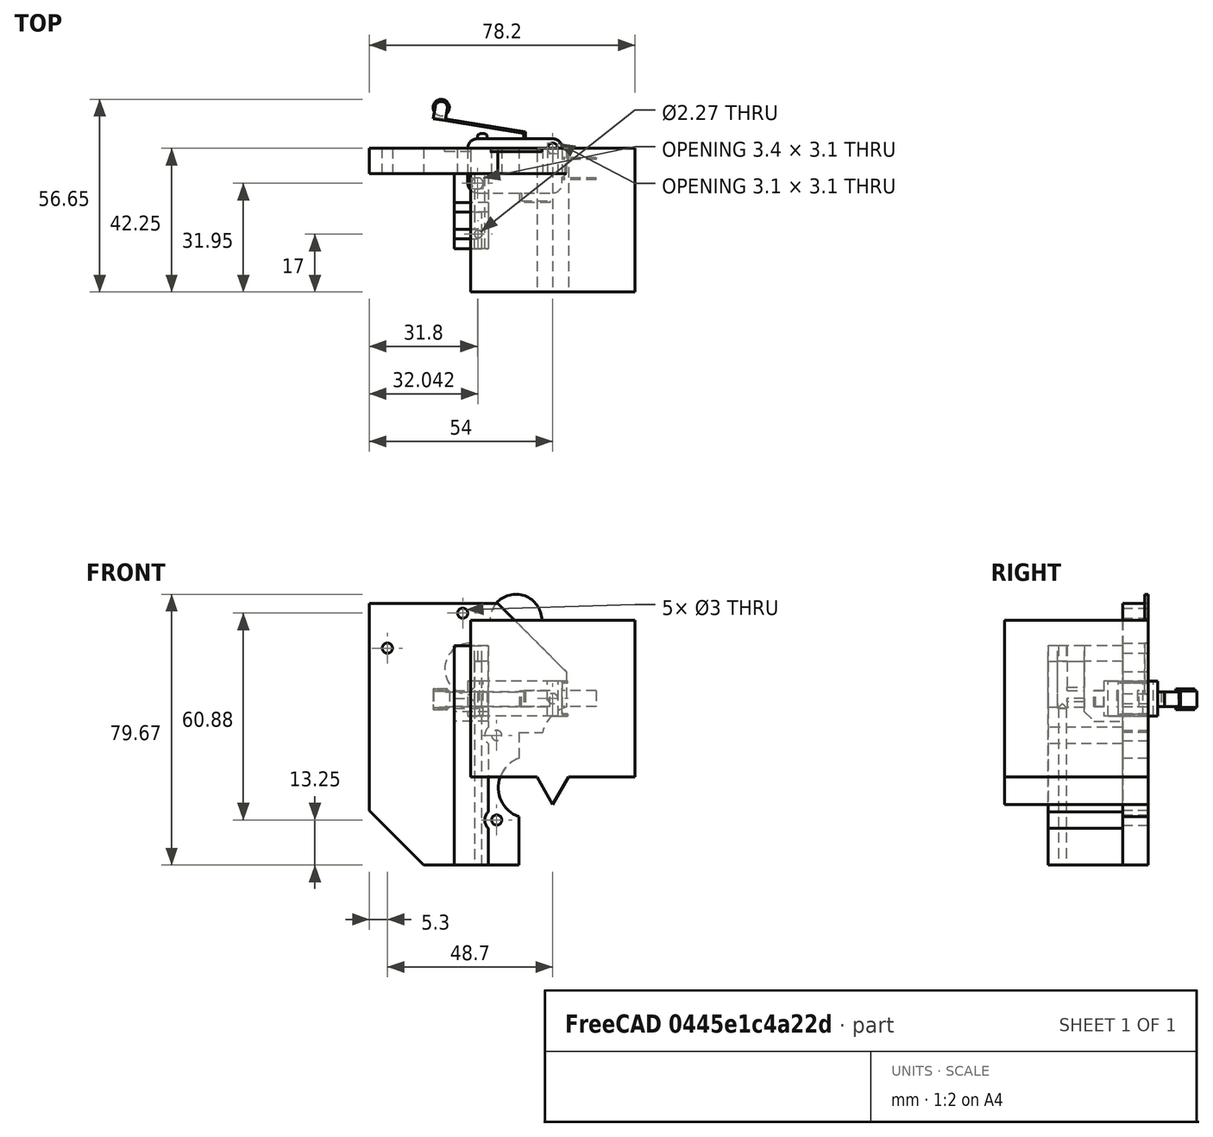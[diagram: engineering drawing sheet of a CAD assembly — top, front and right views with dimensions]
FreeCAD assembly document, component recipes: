
FREECAD ASSEMBLY — COMPONENT RECIPES ("no_touchy")

This assembly document has 5 components, labeled P0..P4 below (a component is one placed body or linked part). 2 of them carry a construction recipe — the FreeCAD feature program that regenerates the part from scratch, quoted from this document or its linked companion documents; the rest are supplied as boundary geometry only. No exploded tour is included for this assembly.
COMPONENT P0 — geometry summary ("allen"; no construction recipe available for this part):
  bounding box: 74.1 x 15.9 x 1.5 mm
  tessellated surface: 68 triangles
  volume: 478904856520590275852955231166615715246145621785509215956463249338484086506495282965888048924409776630849818438009607219283139737538738958728098922627072 mm^3 (27643994136273034751166802490876510581696525263799634684042413042340372770473193175274414860802890257049373180057316332820426398488878841318054540869632% of its bounding box)
  symmetry: mirror-symmetric across its z mid-plane
COMPONENT P1 — recipe-attached ("ender_3_fan_shroud", modeled in this document).
Construction recipe (the document's own serialized feature program — sketch geometry with constraints, then the solid features built on it; lengths are millimeters unless a unit is written):

FEATURE [Sketcher::SketchObject] Sketch004
  MapMode = 1
  Placement = pos=(0,0,0) rot=(1,0,0;1.5708rad)
  sketch-geometry (11):
    g0: LineSegment StartX=-24.2 StartY=23.075 StartZ=0 EndX=-18.45 EndY=23.075 EndZ=0
    g1: LineSegment StartX=24.2 StartY=23.075 StartZ=0 EndX=24.2 EndY=-23.075 EndZ=0
    g2: LineSegment StartX=24.2 StartY=-23.075 StartZ=0 EndX=4.67654 EndY=-23.075 EndZ=0
    g3: LineSegment StartX=-24.2 StartY=-23.075 StartZ=0 EndX=-24.2 EndY=1.125 EndZ=0
    g4: ArcOfCircle CenterX=-10.85 CenterY=23.075 CenterZ=0 NormalX=0 NormalY=0 NormalZ=1 AngleXU=0 Radius=7.6 StartAngle=0 EndAngle=3.14159
    g5: LineSegment StartX=-3.25 StartY=23.075 StartZ=0 EndX=24.2 EndY=23.075 EndZ=0
    g6: ArcOfCircle CenterX=-24.2 CenterY=8.725 CenterZ=0 NormalX=0 NormalY=0 NormalZ=1 AngleXU=0 Radius=7.6 StartAngle=1.5708 EndAngle=4.71239
    g7: LineSegment StartX=-24.2 StartY=16.325 StartZ=0 EndX=-24.2 EndY=23.075 EndZ=0
    g8: LineSegment StartX=-4.67654 StartY=-23.075 StartZ=0 EndX=5.338e-13 EndY=-31.175 EndZ=0
    g9: LineSegment StartX=4.67654 StartY=-23.075 StartZ=0 EndX=5.338e-13 EndY=-31.175 EndZ=0
    g10: LineSegment StartX=-4.67654 StartY=-23.075 StartZ=0 EndX=-24.2 EndY=-23.075 EndZ=0
  constraints (32):
    c: Coincident(g5,g1)
    c: Coincident(g1,g2)
    c: Coincident(g10,g3)
    c: Coincident(g7,g0)
    c: Horizontal(g0)
    c: Horizontal(g2)
    c: Vertical(g1)
    c: Vertical(g3)
    c: Tangent(g0,g5)
    c: Horizontal(g5,g4)
    c: Diameter(g4) = 15.2
    c: DistanceX(g0,g1) = 48.4
    c: Coincident(g4,g5)
    c: Coincident(g4,g0)
    c: PointOnObject(g6,g3)
    c: Coincident(g7,g6)
    c: Tangent(g3,g7)
    c: PointOnObject(g3,g6)
    c: Vertical(g6,g6)
    c: Diameter(g6) = 15.2
    c: DistanceY(g10,g0) = 46.15
    c: DistanceX(g0,g0) = 5.75
    c: DistanceY(g7,g7) = 6.75
    c: Coincident(g9,g8)
    c: Coincident(g2,g9)
    c: Coincident(g10,g8)
    c: Tangent(g2,g10)
    c: Angle(g9,g8) = 1.0472
    c: Equal(g9,g8)
    c: Distance(g8,g5) = 54.25
    c: Equal(g2,g10)
    c: Symmetric(g1,g3,g-1)
FEATURE [PartDesign::Pad] Pad001
  Length = 1
  Length2 = 100
  Placement = pos=(0,0,0) rot=(1,0,0;1.5708rad)
  Profile = -> Sketch004
  Type = 0
FEATURE [Sketcher::SketchObject] Sketch006
  ExternalGeometry = -> [Pad001]
  MapMode = 5
  Placement = pos=(0,-1,3e-16) rot=(1,0,0;1.5708rad)
  Support = -> [Pad001]
  sketch-geometry (7):
    g0: LineSegment StartX=-24.2 StartY=23.075 StartZ=0 EndX=24.2 EndY=23.075 EndZ=0
    g1: LineSegment StartX=24.2 StartY=23.075 StartZ=0 EndX=24.2 EndY=-23.075 EndZ=0
    g2: LineSegment StartX=-24.2 StartY=-23.075 StartZ=0 EndX=-24.2 EndY=23.075 EndZ=0
    g3: LineSegment StartX=-24.2 StartY=-23.075 StartZ=0 EndX=-4.67654 EndY=-23.075 EndZ=0
    g4: LineSegment StartX=-4.67654 StartY=-23.075 StartZ=0 EndX=5.338e-13 EndY=-31.175 EndZ=0
    g5: LineSegment StartX=5.338e-13 StartY=-31.175 StartZ=0 EndX=4.67654 EndY=-23.075 EndZ=0
    g6: LineSegment StartX=4.67654 StartY=-23.075 StartZ=0 EndX=24.2 EndY=-23.075 EndZ=0
  constraints (15):
    c: Coincident(g0,g1)
    c: Coincident(g2,g0)
    c: Horizontal(g0)
    c: Vertical(g1)
    c: Coincident(g2,g3)
    c: Coincident(g3,g4)
    c: Coincident(g4,g5)
    c: Coincident(g5,g6)
    c: Coincident(g6,g1)
    c: Coincident(g1,g-4)
    c: Coincident(g5,g-5)
    c: Coincident(g4,g-6)
    c: Coincident(g3,g-7)
    c: Coincident(g2,g-8)
    c: Coincident(g0,g-3)
FEATURE [PartDesign::Pad] Pad003
  BaseFeature = -> Pad001
  Length = 41.25
  Length2 = 100
  Placement = pos=(0,0,0) rot=(1,0,0;1.5708rad)
  Profile = -> Sketch006
  Type = 0
FEATURE [PartDesign::Body] Body001
  Group = -> [Pad001,Sketch004,Sketch006,Pad003]
  Origin = -> Origin009
  Tip = -> Pad003
COMPONENT P2 — geometry summary ("limit_switch"; no construction recipe available for this part):
  bounding box: 48.0 x 30.1 x 10.3 mm
  tessellated surface: 380 triangles
  volume: 10531229166886375367833218790467075027243968238796608645308768968464382942997063844467289304044690295309601693225177005043369266873093713751413007993119692917567389696 mm^3 (70759783561661155036835508914529565986221704150470811669326561292182287791302966392552419513098743421665918382326803244313745572390062196069500436793845928861630464% of its bounding box)
  symmetry: mirror-symmetric across its y mid-plane
COMPONENT P3 — geometry summary ("micro_swiss_direct_drive_backplate"; no construction recipe available for this part):
  bounding box: 90.8 x 60.0 x 3.2 mm
  tessellated surface: 128 triangles
  volume: 2873429139123541841188444806675058272103768550042216090270967831984327951100462688038986050576327031290007893351530426870904369629373984737226610461114368 mm^3 (16491213821775155754527166314603517383818518835042913780849936584284578971568722629976532881193366380947111070735649138382941081930098950302775747018752% of its bounding box)
  symmetry: mirror-symmetric across its y mid-plane
COMPONENT P4 — recipe-attached ("no_touchy", modeled in this document).
Construction recipe (the document's own serialized feature program — sketch geometry with constraints, then the solid features built on it; lengths are millimeters unless a unit is written):

FEATURE [Sketcher::SketchObject] Sketch005
  MapMode = 5
  Placement = pos=(0,0,0) rot=(1,0,0;1.5708rad)
  Support = -> [XZ_Plane008]
  expr: Constraints[40] = -1 * Spreadsheet.limit_switch_hole_offset_x
  expr: Constraints[41] = -1 * Spreadsheet.limit_switch_hole_offset_y - 3
  sketch-geometry (16):
    g0: LineSegment StartX=-10 StartY=-9.95247 StartZ=0 EndX=-10 EndY=-17.609 EndZ=0
    g1: LineSegment StartX=-10 StartY=-49 StartZ=0 EndX=-38 EndY=-49 EndZ=0
    g2: LineSegment StartX=-54 StartY=-33 StartZ=0 EndX=-54 EndY=28 EndZ=0
    g3: LineSegment StartX=-54 StartY=28 StartZ=0 EndX=-16.1525 EndY=28 EndZ=0
    g4: LineSegment StartX=-10 StartY=-34.7961 StartZ=0 EndX=-10 EndY=-49 EndZ=0
    g5: LineSegment StartX=-10 StartY=-9.95247 StartZ=0 EndX=-2.95564 EndY=-9.95247 EndZ=0
    g6: LineSegment StartX=4 StartY=7.84746 StartZ=0 EndX=4 EndY=-2.5 EndZ=0
    g7: Circle CenterX=0 CenterY=0 CenterZ=0 NormalX=0 NormalY=0 NormalZ=1 AngleXU=0 Radius=2.25
    g8: Circle CenterX=-16.5 CenterY=-10.87 CenterZ=0 NormalX=0 NormalY=0 NormalZ=1 AngleXU=0 Radius=2.25
    g9: Circle CenterX=-16.5 CenterY=-35.75 CenterZ=0 NormalX=0 NormalY=0 NormalZ=1 AngleXU=0 Radius=2.25
    g10: ArcOfCircle CenterX=6.97621 CenterY=-12.25 CenterZ=0 NormalX=0 NormalY=0 NormalZ=1 AngleXU=0 Radius=10.1941 StartAngle=1.86706 EndAngle=2.91426
    g11: ArcOfCircle CenterX=-6.87222 CenterY=-26.2026 CenterZ=0 NormalX=0 NormalY=0 NormalZ=1 AngleXU=0 Radius=9.14502 StartAngle=1.91986 EndAngle=4.36332
    g12: LineSegment StartX=-54 StartY=-33 StartZ=0 EndX=-38 EndY=-49 EndZ=0
    g13: LineSegment StartX=-16.1525 StartY=28 StartZ=0 EndX=4 EndY=7.84746 EndZ=0
    g14: Circle CenterX=-26.5 CenterY=25.13 CenterZ=0 NormalX=0 NormalY=0 NormalZ=1 AngleXU=0 Radius=2.25
    g15: Circle CenterX=-48.7 CenterY=14.83 CenterZ=0 NormalX=0 NormalY=0 NormalZ=1 AngleXU=0 Radius=2.25
  constraints (50):
    c: Coincident(g4,g1)
    c: Horizontal(g1)
    c: Vertical(g0)
    c: Vertical(g2)
    c: Horizontal(g3)
    c: Coincident(g3,g2)
    c: Coincident(g5,g0)
    c: Coincident(g10,g6)
    c: Coincident(g10,g5)
    c: Angle(g10) = 1.0472
    c: Vertical(g6)
    c: Horizontal(g5)
    c: DistanceX(g8) = -16.5
    c: DistanceY(g8) = -10.87
    c: Radius(g7) = 2.25
    c: Equal(g8,g7)
    c: DistanceX(g9) = -16.5
    c: DistanceY(g9) = -35.75
    c: Equal(g9,g7)
    c: Coincident(g11,g0)
    c: Angle(g11) = 2.44346
    c: Vertical(g4)
    c: Coincident(g4,g11)
    c: Vertical(g4,g0)
    c: DistanceX(g7) = 0
    c: DistanceY(g7) = 0
    c: DistanceX(g4) = -10
    c: DistanceY(g4) = -34.7961
    c: DistanceX(g11) = -6.87222
    c: DistanceX(g10) = 6.97621
    c: DistanceY(g10) = -12.25
    c: DistanceX(g6) = 4
    c: DistanceY(g6) = -2.5
    c: Coincident(g12,g2)
    c: Coincident(g12,g1)
    c: Angle(g1,g12) = 2.35619
    c: Coincident(g13,g3)
    c: Coincident(g13,g6)
    c: Angle(g3,g13) = 2.35619
    c: Equal(g14,g7)
    c: DistanceX(g14,g8) = 10
    c: DistanceY(g14,g8) = -36
    c: Equal(g15,g7)
    c: DistanceX(g15,g14) = 22.2
    c: DistanceY(g15,g14) = 10.3
    c: DistanceX(g2) = -54
    c: DistanceY(g2) = 28
    c: DistanceX(g1) = -38
    c: DistanceY(g1) = -49
    c: Distance(g13) = 28.5
FEATURE [PartDesign::Pad] Pad002
  Length = 7.5
  Length2 = 100
  Placement = pos=(0,0,0) rot=(1,0,0;1.5708rad)
  Profile = -> Sketch005
  Type = 0
  expr: Length = Spreadsheet.no_touchy_plate_mount_thickness
FEATURE [Sketcher::SketchObject] Sketch007
  ExternalGeometry = -> [Pad002]
  MapMode = 5
  Placement = pos=(0,-7.5,-1.7e-15) rot=(1,0,0;1.5708rad)
  Support = -> [Pad002]
  expr: Constraints[21] = Spreadsheet.no_touchy_allen_block_pad_width
  expr: Constraints[19] = Spreadsheet.no_touchy_allen_block_pad_length
  sketch-geometry (8):
    g0: LineSegment StartX=-29 StartY=15.5 StartZ=0 EndX=-19 EndY=15.5 EndZ=0
    g1: LineSegment StartX=-19 StartY=15.5 StartZ=0 EndX=-19 EndY=-8.42046 EndZ=0
    g2: LineSegment StartX=-19 StartY=-49 StartZ=0 EndX=-29 EndY=-49 EndZ=0
    g3: LineSegment StartX=-29 StartY=-49 StartZ=0 EndX=-29 EndY=15.5 EndZ=0
    g4: ArcOfCircle CenterX=-16.5 CenterY=-10.87 CenterZ=0 NormalX=0 NormalY=0 NormalZ=1 AngleXU=0 Radius=3.5 StartAngle=2.3664 EndAngle=3.91679
    g5: LineSegment StartX=-19 StartY=-13.3194 StartZ=0 EndX=-19 EndY=-33.3005 EndZ=0
    g6: ArcOfCircle CenterX=-16.5 CenterY=-35.75 CenterZ=0 NormalX=0 NormalY=0 NormalZ=1 AngleXU=0 Radius=3.5 StartAngle=2.3664 EndAngle=3.91679
    g7: LineSegment StartX=-19 StartY=-38.1995 StartZ=0 EndX=-19 EndY=-49 EndZ=0
  constraints (22):
    c: Coincident(g0,g1)
    c: Coincident(g7,g2)
    c: Coincident(g2,g3)
    c: Coincident(g3,g0)
    c: Horizontal(g0)
    c: Horizontal(g2)
    c: Vertical(g1)
    c: Vertical(g3)
    c: Horizontal(g2,g-3)
    c: Coincident(g4,g-5)
    c: Coincident(g1,g4)
    c: Coincident(g5,g4)
    c: Tangent(g1,g5)
    c: Coincident(g6,g-4)
    c: Coincident(g5,g6)
    c: Coincident(g7,g6)
    c: Tangent(g5,g7)
    c: Equal(g6,g4)
    c: Radius(g4) = 3.5
    c: DistanceY(g3,g3) = 64.5
    c: DistanceX(g0,g4) = 2.5
    c: DistanceX(g2,g2) = 10
FEATURE [PartDesign::Pad] Pad004
  BaseFeature = -> Pad002
  Length = 22
  Length2 = 100
  Placement = pos=(0,0,0) rot=(1,0,0;1.5708rad)
  Profile = -> Sketch007
  Type = 0
  expr: Length = Spreadsheet.no_touchy_allen_block_pad_height
FEATURE [Sketcher::SketchObject] Sketch008
  ExternalGeometry = -> [Pad004]
  MapMode = 5
  Placement = pos=(0,-1.09e-14,-49) rot=(1,0,0;3.14159rad)
  Support = -> [Pad004]
  expr: Constraints[0] = Spreadsheet.no_touchy_allen_hole_diameter
  sketch-geometry (1):
    g0: Circle CenterX=-21.958 CenterY=25.2495 CenterZ=0 NormalX=0 NormalY=0 NormalZ=1 AngleXU=0 Radius=1.135
  constraints (3):
    c: Diameter(g0) = 2.27
    c: DistanceX(g0,g-3) = 3.95804
    c: DistanceY(g0,g-3) = -25.2495
FEATURE [PartDesign::Pocket] Pocket001  label="Pocket_allen_hole"
  BaseFeature = -> Pad004
  Length = 1
  Length2 = 100
  Placement = pos=(0,0,0) rot=(1,0,0;1.5708rad)
  Profile = -> Sketch008
  Type = 1
FEATURE [Sketcher::SketchObject] Sketch009
  ExternalGeometry = -> [Pocket001]
  MapMode = 5
  Placement = pos=(0,-29.5,1e-16) rot=(1,0,0;1.5708rad)
  Support = -> [Pocket001]
  sketch-geometry (4):
    g0: LineSegment StartX=-20.823 StartY=11 StartZ=0 EndX=-23.093 EndY=11 EndZ=0
    g1: LineSegment StartX=-23.093 StartY=11 StartZ=0 EndX=-23.093 EndY=-1.5 EndZ=0
    g2: LineSegment StartX=-20.823 StartY=-1.5 StartZ=0 EndX=-20.823 EndY=11 EndZ=0
    g3: ArcOfCircle CenterX=-21.958 CenterY=-1.5 CenterZ=0 NormalX=0 NormalY=0 NormalZ=1 AngleXU=0 Radius=1.135 StartAngle=3.14159 EndAngle=6.28319
  constraints (13):
    c: Coincident(g0,g1)
    c: Coincident(g2,g0)
    c: Horizontal(g0)
    c: Vertical(g1)
    c: Vertical(g2)
    c: Vertical(g2,g-3)
    c: Vertical(g1,g-3)
    c: Coincident(g3,g2)
    c: Coincident(g3,g1)
    c: Horizontal(g2,g1)
    c: Horizontal(g1,g3)
    c: DistanceY(g-3,g1) = 47.5
    c: DistanceY(g-3,g0) = 60
FEATURE [PartDesign::Pocket] Pocket002  label="Pocket_allen_short_slot"
  BaseFeature = -> Pocket001
  Length = 22
  Length2 = 100
  Placement = pos=(0,0,0) rot=(1,0,0;1.5708rad)
  Profile = -> Sketch009
  Type = 0
  expr: Length = Spreadsheet.no_touchy_allen_block_pad_height
FEATURE [Sketcher::SketchObject] Sketch010
  ExternalGeometry = -> [Pocket002]
  MapMode = 5
  Placement = pos=(-19,0,0) rot=(0.707107,0,0.707107;3.14159rad)
  Support = -> [Pocket002]
  sketch-geometry (5):
    g0: LineSegment StartX=-3.85471 StartY=18.7661 StartZ=0 EndX=15.5 EndY=18.7661 EndZ=0
    g1: LineSegment StartX=15.5 StartY=18.7661 StartZ=0 EndX=15.5 EndY=7.5 EndZ=0
    g2: LineSegment StartX=15.5 StartY=7.5 StartZ=0 EndX=-6.68553 EndY=7.5 EndZ=0
    g3: LineSegment StartX=-6.68553 StartY=7.5 StartZ=0 EndX=-6.68553 EndY=15.9352 EndZ=0
    g4: LineSegment StartX=-6.68553 StartY=15.9352 StartZ=0 EndX=-3.85471 EndY=18.7661 EndZ=0
  constraints (12):
    c: Coincident(g1,g2)
    c: Horizontal(g0)
    c: Horizontal(g2)
    c: Vertical(g1)
    c: Vertical(g3)
    c: Coincident(g3,g2)
    c: Horizontal(g1,g-4)
    c: Coincident(g1,g0)
    c: Vertical(g1,g-4)
    c: Coincident(g3,g4)
    c: Coincident(g0,g4)
    c: Angle(g3,g4) = 2.35619
FEATURE [PartDesign::Pocket] Pocket003  label="Pocket_limit_switch_actuator"
  BaseFeature = -> Pocket002
  Length = 5
  Length2 = 100
  Placement = pos=(0,0,0) rot=(1,0,0;1.5708rad)
  Profile = -> Sketch010
  Type = 1
FEATURE [Sketcher::SketchObject] Sketch011
  ExternalGeometry = -> [Pocket003]
  MapMode = 5
  Placement = pos=(-29,0,0) rot=(0.707107,0,-0.707107;3.14159rad)
  Support = -> [Pocket003]
  sketch-geometry (4):
    g0: LineSegment StartX=-15.5 StartY=23.8145 StartZ=0 EndX=2.935 EndY=23.8145 EndZ=0
    g1: LineSegment StartX=2.935 StartY=23.8145 StartZ=0 EndX=2.935 EndY=26.6845 EndZ=0
    g2: LineSegment StartX=2.935 StartY=26.6845 StartZ=0 EndX=-15.5 EndY=26.6845 EndZ=0
    g3: LineSegment StartX=-15.5 StartY=26.6845 StartZ=0 EndX=-15.5 EndY=23.8145 EndZ=0
  constraints (7):
    c: Coincident(g0,g1)
    c: Coincident(g1,g2)
    c: Coincident(g2,g3)
    c: Coincident(g3,g0)
    c: Horizontal(g0)
    c: Vertical(g1)
    c: Vertical(g3)
FEATURE [PartDesign::Pocket] Pocket004  label="Pocket_allen_insert_1"
  BaseFeature = -> Pocket003
  Length = 7
  Length2 = 100
  Placement = pos=(0,0,0) rot=(1,0,0;1.5708rad)
  Profile = -> Sketch011
  Type = 0
FEATURE [Sketcher::SketchObject] Sketch012
  ExternalGeometry = -> [Pocket004]
  MapMode = 5
  Placement = pos=(-29,0,0) rot=(0.707107,0,-0.707107;3.14159rad)
  Support = -> [Pocket004]
  expr: Constraints[10] = Spreadsheet.no_touchy_allen_hole_diameter
  sketch-geometry (4):
    g0: LineSegment StartX=-2.335 StartY=18.7661 StartZ=0 EndX=-0.065 EndY=18.7661 EndZ=0
    g1: LineSegment StartX=-0.065 StartY=18.7661 StartZ=0 EndX=-0.065 EndY=23.8145 EndZ=0
    g2: LineSegment StartX=-0.065 StartY=23.8145 StartZ=0 EndX=-2.335 EndY=23.8145 EndZ=0
    g3: LineSegment StartX=-2.335 StartY=23.8145 StartZ=0 EndX=-2.335 EndY=18.7661 EndZ=0
  constraints (12):
    c: Coincident(g0,g1)
    c: Coincident(g1,g2)
    c: Coincident(g2,g3)
    c: Coincident(g3,g0)
    c: Horizontal(g0)
    c: Horizontal(g2)
    c: Vertical(g1)
    c: Vertical(g3)
    c: Horizontal(g1,g-3)
    c: Horizontal(g0,g-4)
    c: DistanceX(g2,g2) = 2.27
    c: DistanceX(g1,g-3) = 3
FEATURE [PartDesign::Pocket] Pocket005  label="Pocket_allen_insert_2"
  BaseFeature = -> Pocket004
  Length = 5
  Length2 = 100
  Placement = pos=(0,0,0) rot=(1,0,0;1.5708rad)
  Profile = -> Sketch012
  Type = 2
FEATURE [PartDesign::Chamfer] Chamfer
  Angle = 45
  Base = -> Pocket005 [Edge145]
  BaseFeature = -> Pocket005
  ChamferType = 0
  FlipDirection = false
  Placement = pos=(0,0,0) rot=(1,0,0;1.5708rad)
  Size = 1
  Size2 = 1
  SupportTransform = false
FEATURE [PartDesign::Chamfer] Chamfer001
  Angle = 45
  Base = -> Chamfer [Edge59]
  BaseFeature = -> Chamfer
  ChamferType = 0
  FlipDirection = false
  Placement = pos=(0,0,0) rot=(1,0,0;1.5708rad)
  Size = 1
  Size2 = 1
  SupportTransform = false
FEATURE [Sketcher::SketchObject] Sketch013
  ExternalGeometry = -> [Chamfer001]
  MapMode = 5
  Placement = pos=(0,-7.5,1.7e-15) rot=(1,0,0;1.5708rad)
  Support = -> [Chamfer001]
  sketch-geometry (4):
    g0: LineSegment StartX=-23.093 StartY=15.5 StartZ=0 EndX=-19 EndY=15.5 EndZ=0
    g1: LineSegment StartX=-19 StartY=15.5 StartZ=0 EndX=-19 EndY=11 EndZ=0
    g2: LineSegment StartX=-19 StartY=11 StartZ=0 EndX=-23.093 EndY=11 EndZ=0
    g3: LineSegment StartX=-23.093 StartY=11 StartZ=0 EndX=-23.093 EndY=15.5 EndZ=0
  constraints (10):
    c: Coincident(g0,g1)
    c: Coincident(g1,g2)
    c: Coincident(g2,g3)
    c: Coincident(g3,g0)
    c: Horizontal(g0)
    c: Horizontal(g2)
    c: Vertical(g1)
    c: Vertical(g3)
    c: Coincident(g0,g-3)
    c: Coincident(g2,g-4)
FEATURE [PartDesign::Pad] Pad005  label="Pad_support_allen_block"
  BaseFeature = -> Chamfer001
  Length = 10
  Length2 = 100
  Placement = pos=(0,0,0) rot=(1,0,0;1.5708rad)
  Profile = -> Sketch013
  Type = 2
FEATURE [PartDesign::Body] Body
  Group = -> [Sketch005,Pad002,Sketch007,Pad004,Sketch008,Pocket001,Sketch009,Pocket002,Sketch010,Pocket003,Sketch011,Pocket004,Sketch012,Pocket005,Chamfer,Chamfer001,Sketch013,Pad005]
  Origin = -> Origin008
  Tip = -> Pad005
PROVENANCE & LICENSES
A FreeCAD (.FCStd) document from a public repository crawl; recipes are the document's own serialized feature recipes (and, for linked parts, companion documents' recipes).
License: apache-2.0.
